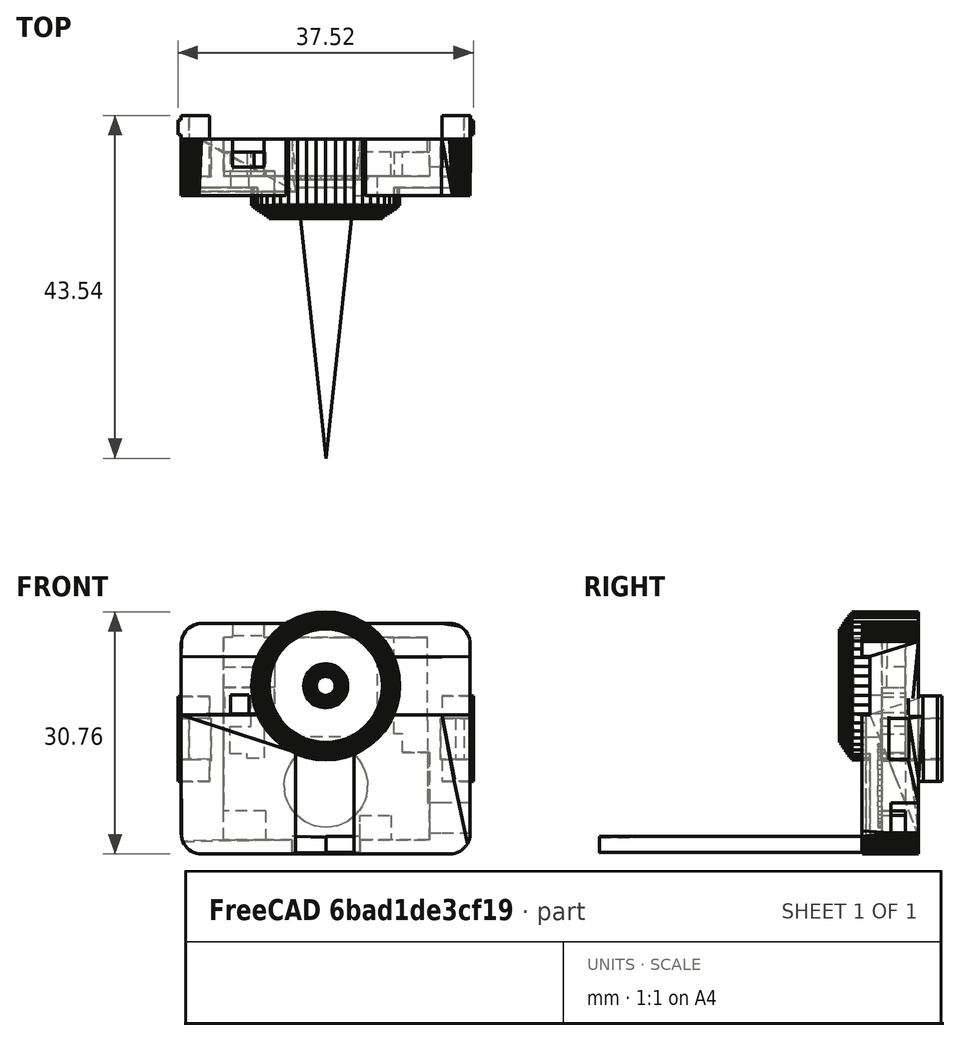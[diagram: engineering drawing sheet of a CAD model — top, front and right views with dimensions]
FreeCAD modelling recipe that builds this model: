
FCSTD DOCUMENT  (FreeCAD 0.16R6706 (Git))
Label: CaseAndDial
License: All rights reserved
LicenseURL: http://en.wikipedia.org/wiki/All_rights_reserved
objects: Part::Extrusion×8, Part::Feature×3, Part::Part2DObjectPython×3, Part::MultiFuse×1, Part::Loft×1
note: 16 computed .brp shape members not serialized (recipe doc carries the construction recipe); baked Part::Feature solids carry a one-line shape summary decoded from their .brp

FEATURE [Part::Feature] purethermal_case_f2_1001_solid  label="purethermal_case_f2_1001 (Solid)"
  shape: bbox 37.51 x 13.05 x 30.76 mm, 4666 faces (baked)
FEATURE [Part::Part2DObjectPython] Line  # Draft 2D object (typed FeaturePython)
  ChamferSize = 0
  Closed = false
  End = (373.614,-9.766,67.7)
  FilletRadius = 0
  Length = 8.586
  MakeFace = true
  Points = (2) [(365.028,-9.766,67.7),(373.614,-9.766,67.7)]
  Start = (365.028,-9.766,67.7)
  Subdivisions = 0
FEATURE [Part::Part2DObjectPython] Line002  # Draft 2D object (typed FeaturePython)
  ChamferSize = 0
  Closed = false
  End = (369.321,-50.3044,67.7)
  FilletRadius = 0
  Length = 40.7651
  MakeFace = true
  Points = (2) [(373.614,-9.766,67.7),(369.321,-50.3044,67.7)]
  Start = (373.614,-9.766,67.7)
  Subdivisions = 0
FEATURE [Part::Part2DObjectPython] Line003  # Draft 2D object (typed FeaturePython)
  ChamferSize = 0
  Closed = false
  End = (365.028,-9.766,67.7)
  FilletRadius = 0
  Length = 40.7652
  MakeFace = true
  Points = (2) [(369.321,-50.3044,67.6),(365.028,-9.766,67.7)]
  Start = (369.321,-50.3044,67.6)
  Subdivisions = 0
FEATURE [Part::Extrusion] Extrude
  Base = -> Line
  Dir = (0,0,2)
  Solid = true
FEATURE [Part::Extrusion] Extrude001
  Base = -> Line002
  Dir = (0,0,2)
  Solid = true
FEATURE [Part::Extrusion] Extrude002
  Base = -> Line003
  Dir = (0,0,2)
  Solid = true
FEATURE [Part::Extrusion] Extrude003
  Base = -> Line
  Dir = (0,0,2)
  Solid = true
FEATURE [Part::Extrusion] Extrude004
  Base = -> Line002
  Dir = (0,0,2)
  Solid = true
FEATURE [Part::Extrusion] Extrude005
  Base = -> Line003
  Dir = (0,0,2)
  Solid = true
FEATURE [Part::Feature] Extrude002_solid  label="Extrude002 (Solid)"
  shape: bbox 4.293 x 40.54 x 2.1 mm, 1 faces (baked)
FEATURE [Part::Feature] Extrude001_solid  label="Extrude001 (Solid)"
  shape: bbox 4.293 x 40.54 x 2 mm, 1 faces (baked)
FEATURE [Part::MultiFuse] Fusion
  Shapes = -> [Extrude002,Extrude001]
FEATURE [Part::Loft] Loft
  Closed = false
  Ruled = false
  Sections = -> [Line002,Line003]
  Solid = false
FEATURE [Part::Extrusion] Extrude006
  Base = -> Loft
  Dir = (0,0,2)
  Solid = false
FEATURE [Part::Extrusion] Extrude007
  Base = -> Loft
  Dir = (0,0,2)
  Solid = false
